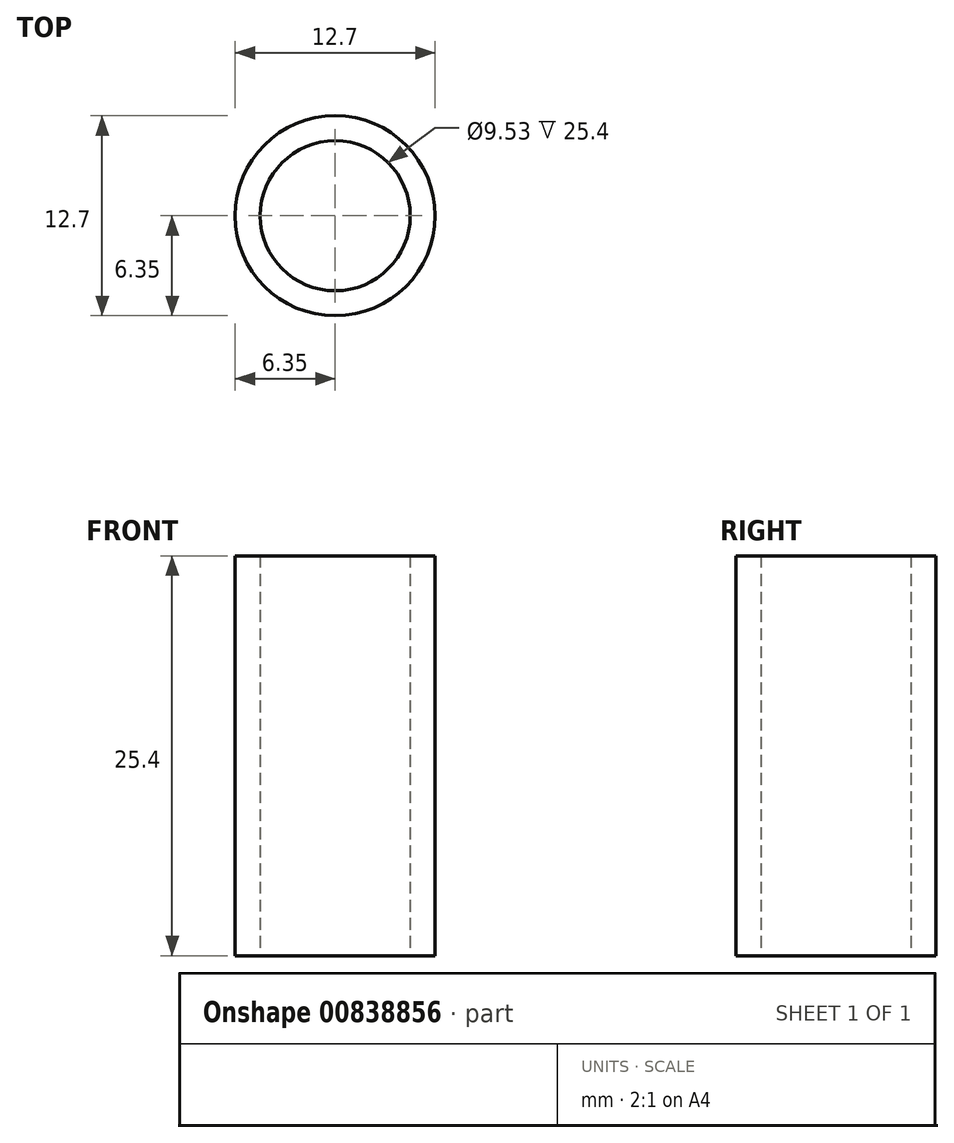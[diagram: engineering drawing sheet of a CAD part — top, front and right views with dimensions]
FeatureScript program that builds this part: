
annotation { "Feature Type Name" : "Feature", "Feature Type Description" : "" }
export const myFeature = defineFeature(function(context is Context, id is Id, definition is map)
    precondition{}
    {
        {
            var Q0;
            Q0=qCreatedBy(makeId("Top.planeOp"),FACE);
            var sketch = newSketch(context, id + "F0", { "sketchPlane" : qUnion([Q0])});
            skCircle(sketch, "E0", {"center": v(0, 0) * mm, "radius": 6.35 * mm});
            skCircle(sketch, "E1", {"center": v(0, 0) * mm, "radius": 4.76 * mm});
            skSolve(sketch);
        }
        {
            var Q0;
            Q0 = qSketchRegion(id + "F0", true);
            extrude(context, id + "F1", {"entities" : qUnion([Q0]), "depth" : 25.4 * mm, "offsetDistance" : 25.4 * mm});
        }
    });
